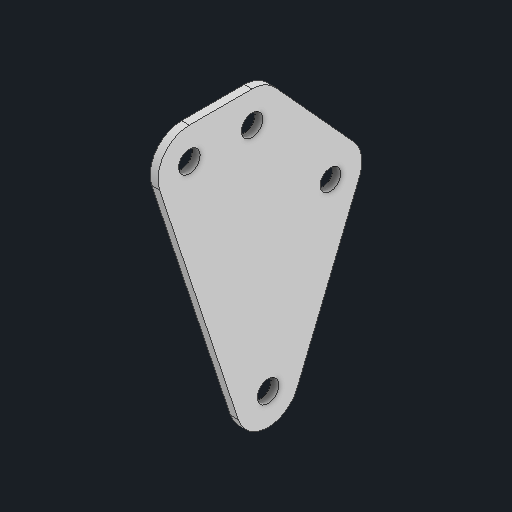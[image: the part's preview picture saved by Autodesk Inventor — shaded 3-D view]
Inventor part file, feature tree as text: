
AUTODESK INVENTOR PART (.ipt)
format: ipt  version: 2025 (Build 290162000, 162)  size: 110,592 bytes
history: native  units: in
note: dims shown in document units (in); Inventor stores cm internally (conversion verified against a paired STEP export)
features: other x3, extrude x1, sketch x1
ambient origin geometry x8: Origin, YZ Plane, XZ Plane, XY Plane, X Axis, Y Axis, Z Axis, Center Point
bodies: Solid1 (feature_tree)
feature tree (5):
  other  "Blocks"
  extrude  "Extrusion1"  Depth=0.5in
  sketch  "Sketch1"  dims[d0=0.5in d1=0.5in d2=0.165in d3=0.172in d4=0.0625in d5=0.0in]
  other  "maiin"
  other  "maiin:1"
